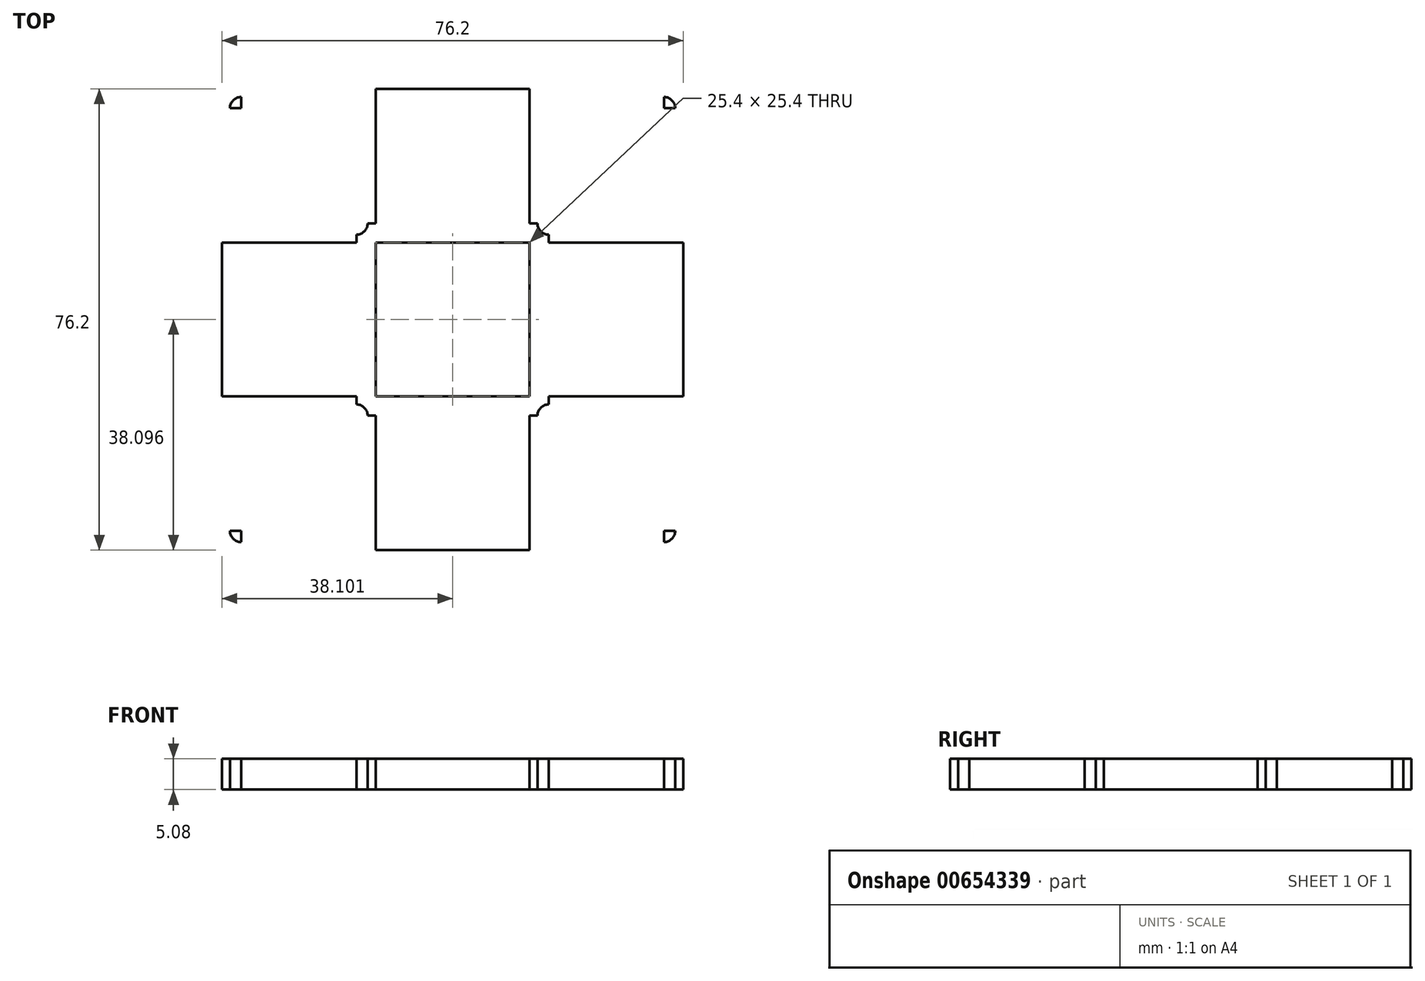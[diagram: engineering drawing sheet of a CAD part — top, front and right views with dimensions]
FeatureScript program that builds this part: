
annotation { "Feature Type Name" : "Feature", "Feature Type Description" : "" }
export const myFeature = defineFeature(function(context is Context, id is Id, definition is map)
    precondition{}
    {
        {
            var Q0;
            Q0=qCreatedBy(makeId("Top.planeOp"),FACE);
            var sketch = newSketch(context, id + "F0", { "sketchPlane" : qUnion([Q0])});
            skLineSegment(sketch, "E0.bottom", {"start": v(-34.18, 31.17) * mm, "end": v(42.02, 31.17) * mm});
            skLineSegment(sketch, "E0.top", {"start": v(-34.18, -45.03) * mm, "end": v(42.02, -45.03) * mm});
            skLineSegment(sketch, "E0.left", {"start": v(-34.18, 31.17) * mm, "end": v(-34.18, -45.03) * mm});
            skLineSegment(sketch, "E0.right", {"start": v(42.02, 31.17) * mm, "end": v(42.02, -45.03) * mm});
            skLineSegment(sketch, "E1.bottom", {"start": v(-34.18, 31.17) * mm, "end": v(-8.78, 31.17) * mm});
            skLineSegment(sketch, "E1.top", {"start": v(-34.18, 5.77) * mm, "end": v(-8.78, 5.77) * mm});
            skLineSegment(sketch, "E1.left", {"start": v(-34.18, 31.17) * mm, "end": v(-34.18, 5.77) * mm});
            skLineSegment(sketch, "E1.right", {"start": v(-8.78, 31.17) * mm, "end": v(-8.78, 5.77) * mm});
            skLineSegment(sketch, "E2.bottom", {"start": v(42.02, 31.17) * mm, "end": v(16.62, 31.17) * mm});
            skLineSegment(sketch, "E2.top", {"start": v(42.02, 5.77) * mm, "end": v(16.62, 5.77) * mm});
            skLineSegment(sketch, "E2.left", {"start": v(42.02, 31.17) * mm, "end": v(42.02, 5.77) * mm});
            skLineSegment(sketch, "E2.right", {"start": v(16.62, 31.17) * mm, "end": v(16.62, 5.77) * mm});
            skLineSegment(sketch, "E3.bottom", {"start": v(-34.18, -45.03) * mm, "end": v(-8.78, -45.03) * mm});
            skLineSegment(sketch, "E3.top", {"start": v(-34.18, -19.63) * mm, "end": v(-8.78, -19.63) * mm});
            skLineSegment(sketch, "E3.left", {"start": v(-34.18, -45.03) * mm, "end": v(-34.18, -19.63) * mm});
            skLineSegment(sketch, "E3.right", {"start": v(-8.78, -45.03) * mm, "end": v(-8.78, -19.63) * mm});
            skLineSegment(sketch, "E4.bottom", {"start": v(42.02, -45.03) * mm, "end": v(16.62, -45.03) * mm});
            skLineSegment(sketch, "E4.top", {"start": v(42.02, -19.63) * mm, "end": v(16.62, -19.63) * mm});
            skLineSegment(sketch, "E4.left", {"start": v(42.02, -45.03) * mm, "end": v(42.02, -19.63) * mm});
            skLineSegment(sketch, "E4.right", {"start": v(16.62, -45.03) * mm, "end": v(16.62, -19.63) * mm});
            skLineSegment(sketch, "E5.bottom", {"start": v(-8.78, 5.77) * mm, "end": v(16.62, 5.77) * mm});
            skLineSegment(sketch, "E5.top", {"start": v(-8.78, -19.63) * mm, "end": v(16.62, -19.63) * mm});
            skLineSegment(sketch, "E5.left", {"start": v(-8.78, 5.77) * mm, "end": v(-8.78, -19.63) * mm});
            skLineSegment(sketch, "E5.right", {"start": v(16.62, 5.77) * mm, "end": v(16.62, -19.63) * mm});
            skLineSegment(sketch, "E6.bottom", {"start": v(-8.78, 5.77) * mm, "end": v(-11.95, 5.77) * mm});
            skLineSegment(sketch, "E6.top", {"start": v(-8.78, 8.94) * mm, "end": v(-11.95, 8.94) * mm});
            skLineSegment(sketch, "E6.left", {"start": v(-8.78, 5.77) * mm, "end": v(-8.78, 8.94) * mm});
            skLineSegment(sketch, "E6.right", {"start": v(-11.95, 5.77) * mm, "end": v(-11.95, 8.94) * mm});
            skLineSegment(sketch, "E7.bottom", {"start": v(16.62, 5.77) * mm, "end": v(19.8, 5.77) * mm});
            skLineSegment(sketch, "E7.top", {"start": v(16.62, 8.94) * mm, "end": v(19.8, 8.94) * mm});
            skLineSegment(sketch, "E7.left", {"start": v(16.62, 5.77) * mm, "end": v(16.62, 8.94) * mm});
            skLineSegment(sketch, "E7.right", {"start": v(19.8, 5.77) * mm, "end": v(19.8, 8.94) * mm});
            skLineSegment(sketch, "E8.bottom", {"start": v(16.62, -19.63) * mm, "end": v(19.8, -19.63) * mm});
            skLineSegment(sketch, "E8.top", {"start": v(16.62, -22.8) * mm, "end": v(19.8, -22.8) * mm});
            skLineSegment(sketch, "E8.left", {"start": v(16.62, -19.63) * mm, "end": v(16.62, -22.8) * mm});
            skLineSegment(sketch, "E8.right", {"start": v(19.8, -19.63) * mm, "end": v(19.8, -22.8) * mm});
            skLineSegment(sketch, "E9.bottom", {"start": v(-8.78, -19.63) * mm, "end": v(-11.95, -19.63) * mm});
            skLineSegment(sketch, "E9.top", {"start": v(-8.78, -22.8) * mm, "end": v(-11.95, -22.8) * mm});
            skLineSegment(sketch, "E9.left", {"start": v(-8.78, -19.63) * mm, "end": v(-8.78, -22.8) * mm});
            skLineSegment(sketch, "E9.right", {"start": v(-11.95, -19.63) * mm, "end": v(-11.95, -22.8) * mm});
            skCircle(sketch, "E10", {"center": v(-11.95, 8.94) * mm, "radius": 1.84 * mm});
            skCircle(sketch, "E11", {"center": v(-11.95, -22.8) * mm, "radius": 1.84 * mm});
            skCircle(sketch, "E12", {"center": v(19.8, -22.8) * mm, "radius": 1.84 * mm});
            skCircle(sketch, "E13", {"center": v(19.8, 8.94) * mm, "radius": 1.84 * mm});
            skLineSegment(sketch, "E14.bottom", {"start": v(-34.18, 31.17) * mm, "end": v(-31, 31.17) * mm});
            skLineSegment(sketch, "E14.top", {"start": v(-34.18, 28) * mm, "end": v(-31, 28) * mm});
            skLineSegment(sketch, "E14.left", {"start": v(-34.18, 31.17) * mm, "end": v(-34.18, 28) * mm});
            skLineSegment(sketch, "E14.right", {"start": v(-31, 31.17) * mm, "end": v(-31, 28) * mm});
            skLineSegment(sketch, "E15.bottom", {"start": v(42.02, 31.17) * mm, "end": v(38.85, 31.17) * mm});
            skLineSegment(sketch, "E15.top", {"start": v(42.02, 28) * mm, "end": v(38.85, 28) * mm});
            skLineSegment(sketch, "E15.left", {"start": v(42.02, 31.17) * mm, "end": v(42.02, 28) * mm});
            skLineSegment(sketch, "E15.right", {"start": v(38.85, 31.17) * mm, "end": v(38.85, 28) * mm});
            skLineSegment(sketch, "E16.bottom", {"start": v(42.02, -45.03) * mm, "end": v(38.85, -45.03) * mm});
            skLineSegment(sketch, "E16.top", {"start": v(42.02, -41.86) * mm, "end": v(38.85, -41.86) * mm});
            skLineSegment(sketch, "E16.left", {"start": v(42.02, -45.03) * mm, "end": v(42.02, -41.86) * mm});
            skLineSegment(sketch, "E16.right", {"start": v(38.85, -45.03) * mm, "end": v(38.85, -41.86) * mm});
            skLineSegment(sketch, "E17.bottom", {"start": v(-34.18, -45.03) * mm, "end": v(-31, -45.03) * mm});
            skLineSegment(sketch, "E17.top", {"start": v(-34.18, -41.86) * mm, "end": v(-31, -41.86) * mm});
            skLineSegment(sketch, "E17.left", {"start": v(-34.18, -45.03) * mm, "end": v(-34.18, -41.86) * mm});
            skLineSegment(sketch, "E17.right", {"start": v(-31, -45.03) * mm, "end": v(-31, -41.86) * mm});
            skCircle(sketch, "E18", {"center": v(38.85, -41.86) * mm, "radius": 1.84 * mm});
            skCircle(sketch, "E19", {"center": v(38.85, 28) * mm, "radius": 1.84 * mm});
            skCircle(sketch, "E20", {"center": v(-31, 28) * mm, "radius": 1.84 * mm});
            skCircle(sketch, "E21", {"center": v(-31, -41.86) * mm, "radius": 1.84 * mm});
            skLineSegment(sketch, "E22.bottom", {"start": v(-34.18, 31.17) * mm, "end": v(-59.58, 31.17) * mm});
            skLineSegment(sketch, "E22.top", {"start": v(-34.18, 56.57) * mm, "end": v(-59.58, 56.57) * mm});
            skLineSegment(sketch, "E22.left", {"start": v(-34.18, 31.17) * mm, "end": v(-34.18, 56.57) * mm});
            skLineSegment(sketch, "E22.right", {"start": v(-59.58, 31.17) * mm, "end": v(-59.58, 56.57) * mm});
            skLineSegment(sketch, "E23.bottom", {"start": v(42.02, 31.17) * mm, "end": v(67.42, 31.17) * mm});
            skLineSegment(sketch, "E23.top", {"start": v(42.02, 56.57) * mm, "end": v(67.42, 56.57) * mm});
            skLineSegment(sketch, "E23.left", {"start": v(42.02, 31.17) * mm, "end": v(42.02, 56.57) * mm});
            skLineSegment(sketch, "E23.right", {"start": v(67.42, 31.17) * mm, "end": v(67.42, 56.57) * mm});
            skLineSegment(sketch, "E24.bottom", {"start": v(-34.18, -45.03) * mm, "end": v(-59.58, -45.03) * mm});
            skLineSegment(sketch, "E24.top", {"start": v(-34.18, -70.43) * mm, "end": v(-59.58, -70.43) * mm});
            skLineSegment(sketch, "E24.left", {"start": v(-34.18, -45.03) * mm, "end": v(-34.18, -70.43) * mm});
            skLineSegment(sketch, "E24.right", {"start": v(-59.58, -45.03) * mm, "end": v(-59.58, -70.43) * mm});
            skLineSegment(sketch, "E25.bottom", {"start": v(42.02, -45.03) * mm, "end": v(67.42, -45.03) * mm});
            skLineSegment(sketch, "E25.top", {"start": v(42.02, -70.43) * mm, "end": v(67.42, -70.43) * mm});
            skLineSegment(sketch, "E25.left", {"start": v(42.02, -45.03) * mm, "end": v(42.02, -70.43) * mm});
            skLineSegment(sketch, "E25.right", {"start": v(67.42, -45.03) * mm, "end": v(67.42, -70.43) * mm});
            skLineSegment(sketch, "E26.bottom", {"start": v(-34.18, 56.57) * mm, "end": v(42.02, 56.57) * mm});
            skLineSegment(sketch, "E26.left", {"start": v(-34.18, 56.57) * mm, "end": v(-34.18, 31.17) * mm});
            skLineSegment(sketch, "E26.right", {"start": v(42.02, 56.57) * mm, "end": v(42.02, 31.17) * mm});
            skLineSegment(sketch, "E27.right", {"start": v(67.42, 31.17) * mm, "end": v(67.42, -45.03) * mm});
            skLineSegment(sketch, "E28.bottom", {"start": v(-59.58, 31.17) * mm, "end": v(-34.18, 31.17) * mm});
            skLineSegment(sketch, "E28.top", {"start": v(-59.58, -45.03) * mm, "end": v(-34.18, -45.03) * mm});
            skLineSegment(sketch, "E28.left", {"start": v(-59.58, 31.17) * mm, "end": v(-59.58, -45.03) * mm});
            skLineSegment(sketch, "E29.bottom", {"start": v(-34.18, -70.43) * mm, "end": v(42.02, -70.43) * mm});
            skLineSegment(sketch, "E29.left", {"start": v(-34.18, -70.43) * mm, "end": v(-34.18, -45.03) * mm});
            skLineSegment(sketch, "E29.right", {"start": v(42.02, -70.43) * mm, "end": v(42.02, -45.03) * mm});
            skSolve(sketch);
        }
        {
            var Q0;
            {var subQ1=sQuery(id+"F0.wireOp",EDGE,"E1.right");Q0=makeQuery(id+"F0.imprint","IMPRINT",FACE,{"disambiguationData":[TD([[makeQuery(id+"F0.imprint","IMPRINT",EDGE,{"derivedFrom":subQ1}),1.0]])]});}
            var Q1;
            {var subQ10=sQuery(id+"F0.wireOp",EDGE,"E1.top");Q1=makeQuery(id+"F0.imprint","IMPRINT",FACE,{"disambiguationData":[TD([[makeQuery(id+"F0.imprint","IMPRINT",EDGE,{"derivedFrom":subQ10}),1.0]])]});}
            var Q2;
            {var subQ1=sQuery(id+"F0.wireOp",EDGE,"E1.top");Q2=makeQuery(id+"F0.imprint","IMPRINT",FACE,{"disambiguationData":[TD([[makeQuery(id+"F0.imprint","IMPRINT",EDGE,{"derivedFrom":subQ1}),-1.0]])]});}
            var Q3;
            {var subQ5=sQuery(id+"F0.wireOp",EDGE,"E3.top");Q3=makeQuery(id+"F0.imprint","IMPRINT",FACE,{"disambiguationData":[TD([[makeQuery(id+"F0.imprint","IMPRINT",EDGE,{"derivedFrom":subQ5}),-1.0]])]});}
            var Q4;
            {var subQ0=sQuery(id+"F0.wireOp",EDGE,"E3.right");Q4=makeQuery(id+"F0.imprint","IMPRINT",FACE,{"disambiguationData":[TD([[makeQuery(id+"F0.imprint","IMPRINT",EDGE,{"derivedFrom":subQ0}),-1.0]])]});}
            var Q5;
            {var subQ1=sQuery(id+"F0.wireOp",EDGE,"E4.top");Q5=makeQuery(id+"F0.imprint","IMPRINT",FACE,{"disambiguationData":[TD([[makeQuery(id+"F0.imprint","IMPRINT",EDGE,{"derivedFrom":subQ1}),1.0]])]});}
            var Q6;
            {var subQ1=sQuery(id+"F0.wireOp",EDGE,"E2.top");Q6=makeQuery(id+"F0.imprint","IMPRINT",FACE,{"disambiguationData":[TD([[makeQuery(id+"F0.imprint","IMPRINT",EDGE,{"derivedFrom":subQ1}),1.0]])]});}
            var Q7;
            {var subQ12=sQuery(id+"F0.wireOp",EDGE,"E2.top");Q7=makeQuery(id+"F0.imprint","IMPRINT",FACE,{"disambiguationData":[TD([[makeQuery(id+"F0.imprint","IMPRINT",EDGE,{"derivedFrom":subQ12}),-1.0]])]});}
            var Q8;
            {var subQ1=sQuery(id+"F0.wireOp",EDGE,"E7.bottom");Q8=makeQuery(id+"F0.imprint","IMPRINT",FACE,{"disambiguationData":[TD([[makeQuery(id+"F0.imprint","IMPRINT",EDGE,{"derivedFrom":subQ1}),1.0]])]});}
            var Q9;
            {var subQ3=sQuery(id+"F0.wireOp",EDGE,"E0.right");var subQ5=sQuery(id+"F0.wireOp",EDGE,"E15.top");var subQ6=makeQuery(id+"F0.imprint","INTERSECT",VERTEX,{"derivedFrom":[subQ5,subQ3]});Q9=makeQuery(id+"F0.imprint","IMPRINT",FACE,{"disambiguationData":[TD([[makeQuery(id+"F0.imprint","IMPRINT",EDGE,{"disambiguationData":[TD([[subQ6,-1.0]])],"derivedFrom":subQ5}),-1.0]])]});}
            var Q10;
            {var subQ1=sQuery(id+"F0.wireOp",EDGE,"E6.bottom");Q10=makeQuery(id+"F0.imprint","IMPRINT",FACE,{"disambiguationData":[TD([[makeQuery(id+"F0.imprint","IMPRINT",EDGE,{"derivedFrom":subQ1}),-1.0]])]});}
            var Q11;
            {var subQ1=sQuery(id+"F0.wireOp",EDGE,"E9.bottom");Q11=makeQuery(id+"F0.imprint","IMPRINT",FACE,{"disambiguationData":[TD([[makeQuery(id+"F0.imprint","IMPRINT",EDGE,{"derivedFrom":subQ1}),1.0]])]});}
            var Q12;
            {var subQ1=sQuery(id+"F0.wireOp",EDGE,"E8.bottom");Q12=makeQuery(id+"F0.imprint","IMPRINT",FACE,{"disambiguationData":[TD([[makeQuery(id+"F0.imprint","IMPRINT",EDGE,{"derivedFrom":subQ1}),-1.0]])]});}
            var Q13;
            {var subQ3=sQuery(id+"F0.wireOp",EDGE,"E0.left");var subQ5=sQuery(id+"F0.wireOp",EDGE,"E14.top");var subQ6=makeQuery(id+"F0.imprint","INTERSECT",VERTEX,{"derivedFrom":[subQ5,subQ3]});Q13=makeQuery(id+"F0.imprint","IMPRINT",FACE,{"disambiguationData":[TD([[makeQuery(id+"F0.imprint","IMPRINT",EDGE,{"disambiguationData":[TD([[subQ6,-1.0]])],"derivedFrom":subQ5}),1.0]])]});}
            var Q14;
            {var subQ0=sQuery(id+"F0.wireOp",EDGE,"E0.left");var subQ1=sQuery(id+"F0.wireOp",EDGE,"E17.top");var subQ2=makeQuery(id+"F0.imprint","INTERSECT",VERTEX,{"derivedFrom":[subQ1,subQ0]});Q14=makeQuery(id+"F0.imprint","IMPRINT",FACE,{"disambiguationData":[TD([[makeQuery(id+"F0.imprint","IMPRINT",EDGE,{"disambiguationData":[TD([[subQ2,-1.0]])],"derivedFrom":subQ1}),-1.0]])]});}
            var Q15;
            {var subQ0=sQuery(id+"F0.wireOp",EDGE,"E0.right");var subQ1=sQuery(id+"F0.wireOp",EDGE,"E16.top");var subQ2=makeQuery(id+"F0.imprint","INTERSECT",VERTEX,{"derivedFrom":[subQ1,subQ0]});Q15=makeQuery(id+"F0.imprint","IMPRINT",FACE,{"disambiguationData":[TD([[makeQuery(id+"F0.imprint","IMPRINT",EDGE,{"disambiguationData":[TD([[subQ2,-1.0]])],"derivedFrom":subQ1}),1.0]])]});}
            extrude(context, id + "F1", {"entities" : qUnion([Q0, Q1, Q2, Q3, Q4, Q5, Q6, Q7, Q8, Q9, Q10, Q11, Q12, Q13, Q14, Q15]), "depth" : 5.08 * mm, "offsetDistance" : 25.4 * mm});
        }
    });
